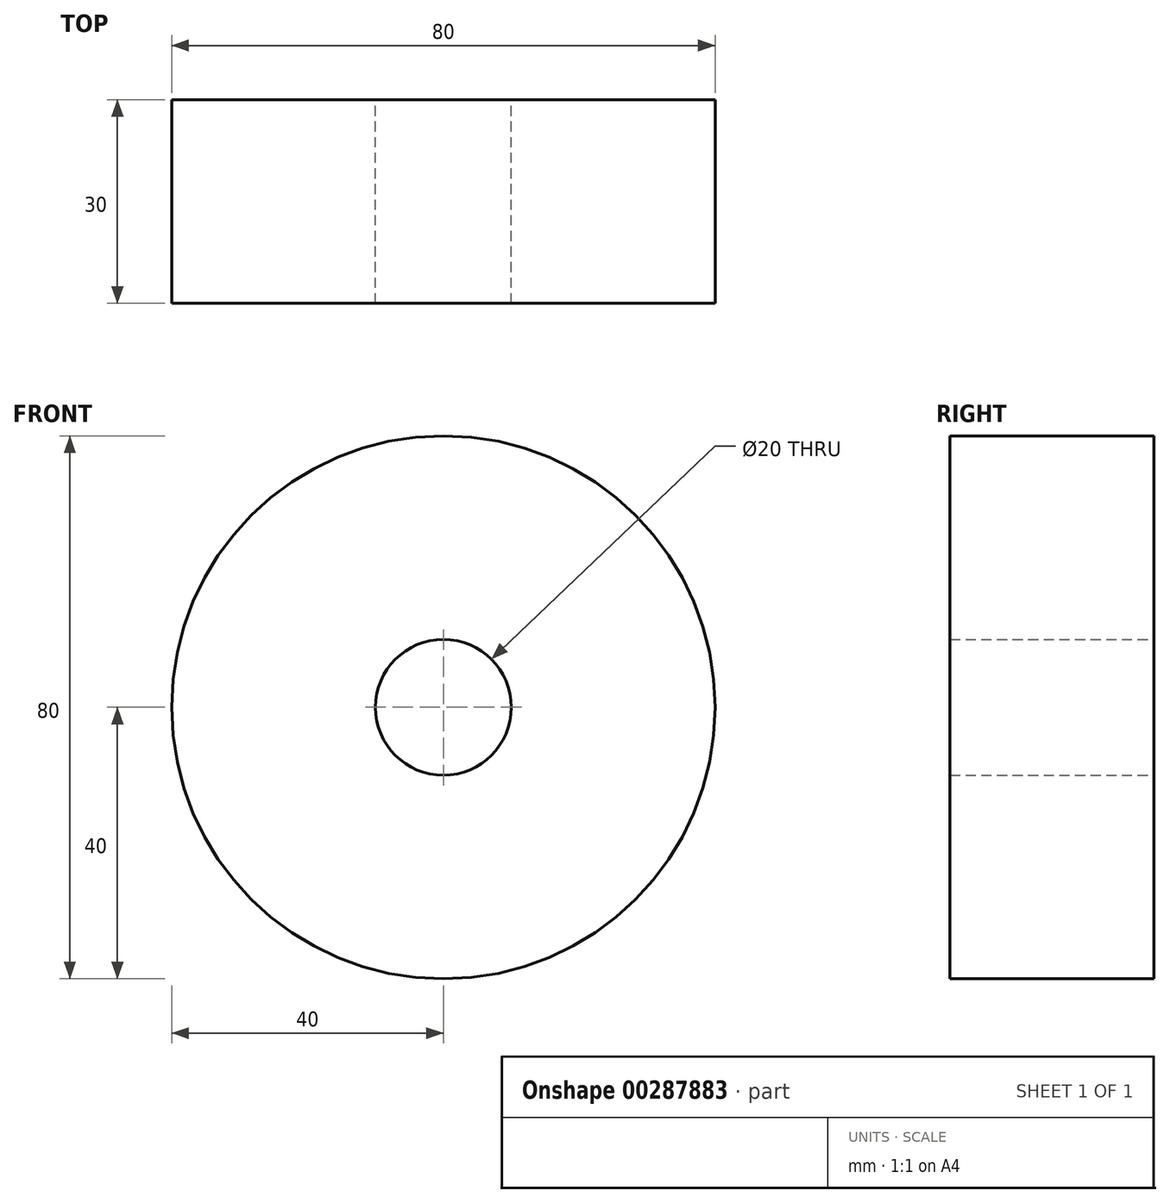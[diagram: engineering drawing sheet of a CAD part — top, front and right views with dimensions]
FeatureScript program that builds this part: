
annotation { "Feature Type Name" : "Feature", "Feature Type Description" : "" }
export const myFeature = defineFeature(function(context is Context, id is Id, definition is map)
    precondition{}
    {
        {
            var Q0;
            Q0=qCreatedBy(makeId("Front.planeOp"),FACE);
            var sketch = newSketch(context, id + "F0", { "sketchPlane" : qUnion([Q0])});
            skCircle(sketch, "E0", {"center": v(0, 0) * mm, "radius": 10 * mm});
            skCircle(sketch, "E1", {"center": v(0, 0) * mm, "radius": 40 * mm});
            skSolve(sketch);
        }
        {
            var Q0;
            Q0 = qSketchRegion(id + "F0", true);
            extrude(context, id + "F1", {"entities" : qUnion([Q0]), "depth" : 30 * mm});
        }
    });
